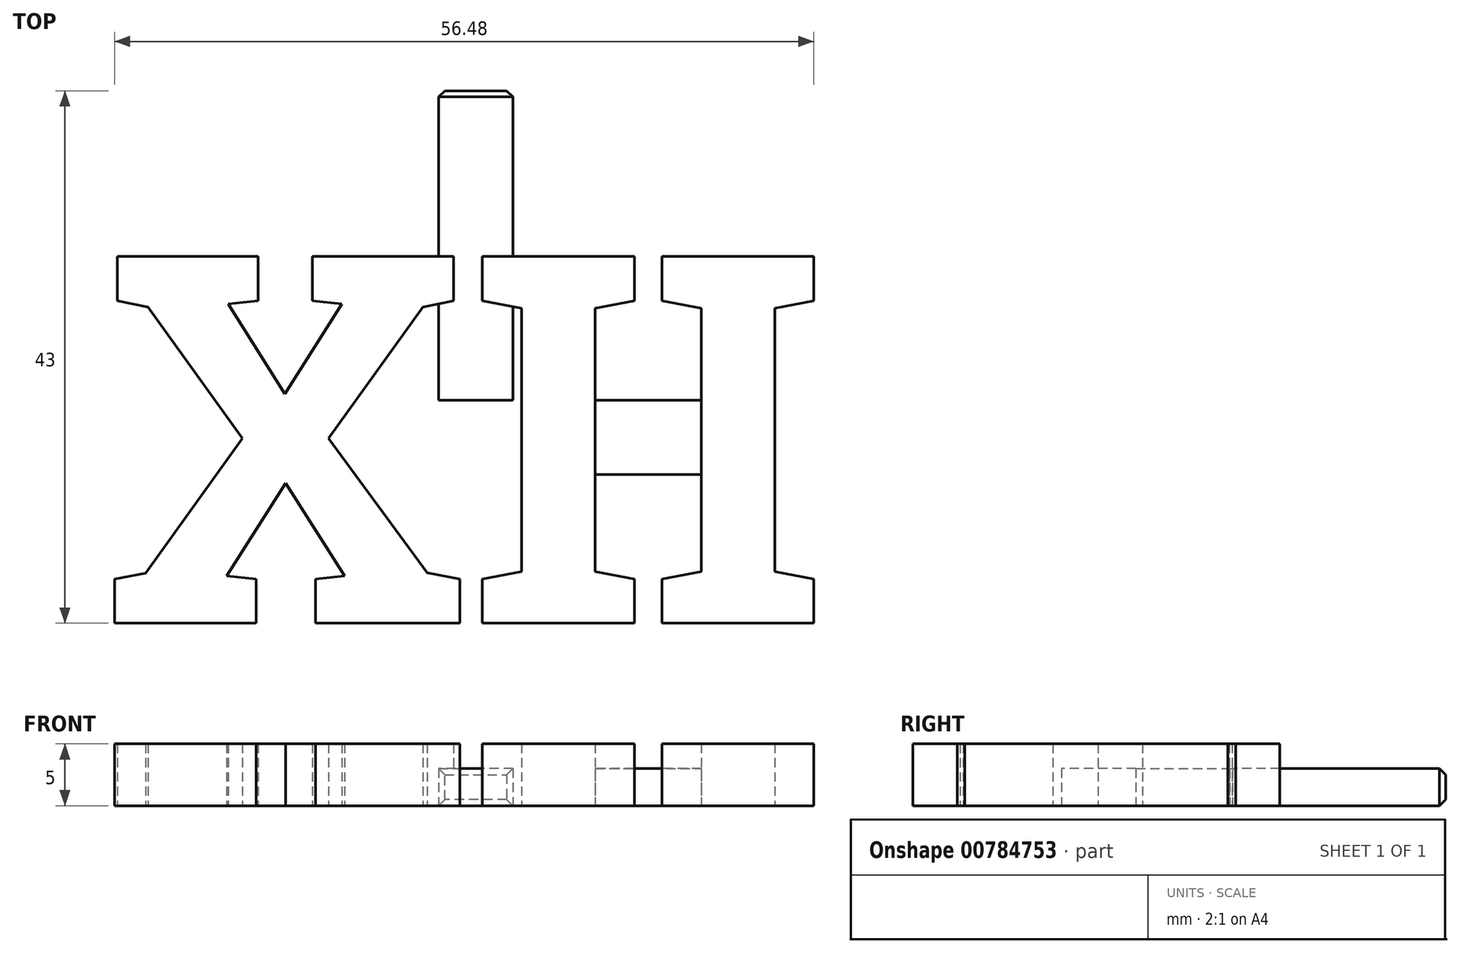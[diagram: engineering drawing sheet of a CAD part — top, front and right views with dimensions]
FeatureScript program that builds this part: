
annotation { "Feature Type Name" : "Feature", "Feature Type Description" : "" }
export const myFeature = defineFeature(function(context is Context, id is Id, definition is map)
    precondition{}
    {
        {
            var Q0;
            Q0=qCreatedBy(makeId("Top.planeOp"),FACE);
            var sketch = newSketch(context, id + "F0", { "sketchPlane" : qUnion([Q0])});
            skLineSegment(sketch, "E0.bottom", {"start": v(-15, 15) * mm, "end": v(15, 15) * mm, "construction": true});
            skText(sketch, "E1", { "text": "XII", "fontName": "RobotoSlab-Bold.ttf"});
            skLineSegment(sketch, "E2.bottom", {"start": v(-3, 3) * mm, "end": v(3, 3) * mm});
            skLineSegment(sketch, "E2.top", {"start": v(-3, 28) * mm, "end": v(3, 28) * mm});
            skLineSegment(sketch, "E2.left", {"start": v(-3, 3) * mm, "end": v(-3, 28) * mm});
            skLineSegment(sketch, "E2.right", {"start": v(3, 3) * mm, "end": v(3, 28) * mm});
            skLineSegment(sketch, "E3", {"start": v(-22.66, 3) * mm, "end": v(25.9, 3) * mm});
            skLineSegment(sketch, "E4", {"start": v(25.9, -3) * mm, "end": v(-22.66, -3) * mm});
            const initialGuessF0  = {"E1": [-0.02985, -0.015, 1, 0, 0.03]};
            skSetInitialGuess(sketch, initialGuessF0);
            skSolve(sketch);
        }
        {
            var Q0;
            {var subQ4=sQuery(id+"F0.wireOp",EDGE,"E1.sketch_text.stroke-3");Q0=makeQuery(id+"F0.imprint","IMPRINT",FACE,{"disambiguationData":[TD([[makeQuery(id+"F0.imprint","IMPRINT",EDGE,{"derivedFrom":subQ4}),-1.0]])]});}
            var Q1;
            {var subQ5=sQuery(id+"F0.wireOp",EDGE,"E1.sketch_text.stroke-2");var subQ6=sQuery(id+"F0.wireOp",EDGE,"E1.sketch_text.stroke-1");var subQ7=makeQuery(id+"F0.imprint","INTERSECT",VERTEX,{"derivedFrom":[subQ6,subQ5]});Q1=makeQuery(id+"F0.imprint","IMPRINT",FACE,{"disambiguationData":[TD([[makeQuery(id+"F0.imprint","IMPRINT",EDGE,{"disambiguationData":[TD([[subQ7,1.0]])],"derivedFrom":subQ6}),-1.0]])]});}
            var Q2;
            {var subQ1=sQuery(id+"F0.wireOp",EDGE,"E1.sketch_text.stroke-0");Q2=makeQuery(id+"F0.imprint","IMPRINT",FACE,{"disambiguationData":[TD([[makeQuery(id+"F0.imprint","IMPRINT",EDGE,{"derivedFrom":subQ1}),-1.0]])]});}
            var Q3;
            {var subQ1=sQuery(id+"F0.wireOp",EDGE,"E1.sketch_text.stroke-0");Q3=makeQuery(id+"F0.imprint","IMPRINT",FACE,{"disambiguationData":[TD([[makeQuery(id+"F0.imprint","IMPRINT",EDGE,{"derivedFrom":subQ1}),-1.0]])]});}
            var Q4;
            {var subQ4=sQuery(id+"F0.wireOp",EDGE,"E1.sketch_text.stroke-3");Q4=makeQuery(id+"F0.imprint","IMPRINT",FACE,{"disambiguationData":[TD([[makeQuery(id+"F0.imprint","IMPRINT",EDGE,{"derivedFrom":subQ4}),-1.0]])]});}
            var Q5;
            {var subQ0=sQuery(id+"F0.wireOp",EDGE,"E1.sketch_text.stroke-13");Q5=makeQuery(id+"F0.imprint","IMPRINT",FACE,{"disambiguationData":[TD([[makeQuery(id+"F0.imprint","IMPRINT",EDGE,{"derivedFrom":subQ0}),-1.0]])]});}
            var Q6;
            {var subQ0=sQuery(id+"F0.wireOp",EDGE,"E1.sketch_text.stroke-28");Q6=makeQuery(id+"F0.imprint","IMPRINT",FACE,{"disambiguationData":[TD([[makeQuery(id+"F0.imprint","IMPRINT",EDGE,{"derivedFrom":subQ0}),-1.0]])]});}
            var Q7;
            {var subQ1=sQuery(id+"F0.wireOp",EDGE,"E1.sketch_text.stroke-30");Q7=makeQuery(id+"F0.imprint","IMPRINT",FACE,{"disambiguationData":[TD([[makeQuery(id+"F0.imprint","IMPRINT",EDGE,{"derivedFrom":subQ1}),-1.0]])]});}
            var Q8;
            {var subQ0=sQuery(id+"F0.wireOp",EDGE,"E4");var subQ1=sQuery(id+"F0.wireOp",EDGE,"E1.sketch_text.stroke-32");var subQ2=makeQuery(id+"F0.imprint","INTERSECT",VERTEX,{"derivedFrom":[subQ1,subQ0]});Q8=makeQuery(id+"F0.imprint","IMPRINT",FACE,{"disambiguationData":[TD([[makeQuery(id+"F0.imprint","IMPRINT",EDGE,{"disambiguationData":[TD([[subQ2,1.0]])],"derivedFrom":subQ1}),-1.0]])]});}
            var Q9;
            {var subQ0=sQuery(id+"F0.wireOp",EDGE,"E1.sketch_text.stroke-33");Q9=makeQuery(id+"F0.imprint","IMPRINT",FACE,{"disambiguationData":[TD([[makeQuery(id+"F0.imprint","IMPRINT",EDGE,{"derivedFrom":subQ0}),-1.0]])]});}
            var Q10;
            {var subQ0=sQuery(id+"F0.wireOp",EDGE,"E1.sketch_text.stroke-45");Q10=makeQuery(id+"F0.imprint","IMPRINT",FACE,{"disambiguationData":[TD([[makeQuery(id+"F0.imprint","IMPRINT",EDGE,{"derivedFrom":subQ0}),-1.0]])]});}
            var Q11;
            {var subQ0=sQuery(id+"F0.wireOp",EDGE,"E4");var subQ1=sQuery(id+"F0.wireOp",EDGE,"E1.sketch_text.stroke-44");var subQ2=makeQuery(id+"F0.imprint","INTERSECT",VERTEX,{"derivedFrom":[subQ1,subQ0]});Q11=makeQuery(id+"F0.imprint","IMPRINT",FACE,{"disambiguationData":[TD([[makeQuery(id+"F0.imprint","IMPRINT",EDGE,{"disambiguationData":[TD([[subQ2,1.0]])],"derivedFrom":subQ1}),-1.0]])]});}
            var Q12;
            Q12=makeQuery(id+"F0.imprint","IMPRINT",FACE,{"disambiguationData":[TD([[makeQuery(id+"F0.imprint","IMPRINT",EDGE,{"derivedFrom":sQuery(id+"F0.wireOp",EDGE,"E1.sketch_text.stroke-40")}),-1.0]])]});
            extrude(context, id + "F1", {"entities" : qUnion([Q0, Q1, Q2, Q3, Q4, Q5, Q6, Q7, Q8, Q9, Q10, Q11, Q12]), "depth" : 5 * mm, "offsetDistance" : 25 * mm});
        }
        {
            var Q0;
            {var subQ0=sQuery(id+"F0.wireOp",EDGE,"E1.sketch_text.stroke-9");var subQ1=sQuery(id+"F0.wireOp",EDGE,"E1.sketch_text.stroke-8");var subQ2=makeQuery(id+"F0.imprint","INTERSECT",VERTEX,{"derivedFrom":[subQ1,subQ0]});Q0=makeQuery(id+"F0.imprint","IMPRINT",FACE,{"disambiguationData":[TD([[makeQuery(id+"F0.imprint","IMPRINT",EDGE,{"disambiguationData":[TD([[subQ2,1.0]])],"derivedFrom":subQ1}),1.0]])]});}
            var Q1;
            {var subQ0=sQuery(id+"F0.wireOp",EDGE,"E1.sketch_text.stroke-23");var subQ1=sQuery(id+"F0.wireOp",EDGE,"E1.sketch_text.stroke-22");var subQ2=makeQuery(id+"F0.imprint","INTERSECT",VERTEX,{"derivedFrom":[subQ1,subQ0]});Q1=makeQuery(id+"F0.imprint","IMPRINT",FACE,{"disambiguationData":[TD([[makeQuery(id+"F0.imprint","IMPRINT",EDGE,{"disambiguationData":[TD([[subQ2,1.0]])],"derivedFrom":subQ1}),1.0]])]});}
            var Q2;
            {var subQ0=sQuery(id+"F0.wireOp",EDGE,"E2.bottom");Q2=makeQuery(id+"F0.imprint","IMPRINT",FACE,{"disambiguationData":[TD([[makeQuery(id+"F0.imprint","IMPRINT",EDGE,{"derivedFrom":subQ0}),-1.0]])]});}
            var Q3;
            {var subQ0=sQuery(id+"F0.wireOp",EDGE,"E4");var subQ1=sQuery(id+"F0.wireOp",EDGE,"E1.sketch_text.stroke-32");var subQ2=makeQuery(id+"F0.imprint","INTERSECT",VERTEX,{"derivedFrom":[subQ1,subQ0]});Q3=makeQuery(id+"F0.imprint","IMPRINT",FACE,{"disambiguationData":[TD([[makeQuery(id+"F0.imprint","IMPRINT",EDGE,{"disambiguationData":[TD([[subQ2,1.0]])],"derivedFrom":subQ1}),1.0]])]});}
            var Q4;
            {var subQ11=sQuery(id+"F0.wireOp",EDGE,"E1.sketch_text.stroke-13");Q4=makeQuery(id+"F0.imprint","IMPRINT",FACE,{"disambiguationData":[TD([[makeQuery(id+"F0.imprint","IMPRINT",EDGE,{"derivedFrom":subQ11}),1.0]])]});}
            extrude(context, id + "F2", {"entities" : qUnion([Q0, Q1, Q2, Q3, Q4]), "operationType" : NewBodyOperationType.ADD, "depth" : 3 * mm, "offsetDistance" : 25 * mm});
        }
        {
            var Q0;
            Q0=makeQuery(id+"F2.opExtrude","SWEPT_EDGE",EDGE,{"disambiguationData":[OSD([sQuery(id+"F0.wireOp",EDGE,"E2.top"),sQuery(id+"F0.wireOp",EDGE,"E2.left")])]});
            var Q1;
            Q1=makeQuery(id+"F2.opExtrude","SWEPT_EDGE",EDGE,{"disambiguationData":[OSD([sQuery(id+"F0.wireOp",EDGE,"E2.top"),sQuery(id+"F0.wireOp",EDGE,"E2.right")])]});
            var Q2;
            Q2=makeQuery(id+"F2.opExtrude","CAP_EDGE",EDGE,{"disambiguationData":[OSD([sQuery(id+"F0.wireOp",EDGE,"E2.top")])],"isStart":false});
            var Q3;
            Q3=makeQuery(id+"F2.opExtrude","CAP_EDGE",EDGE,{"disambiguationData":[OSD([sQuery(id+"F0.wireOp",EDGE,"E2.top")])],"isStart":true});
            chamfer(context, id + "F3", {"entities" : qUnion([Q0, Q1, Q2, Q3]), "width" : 0.5 * mm, "tangentPropagation" : true});
        }
    });
